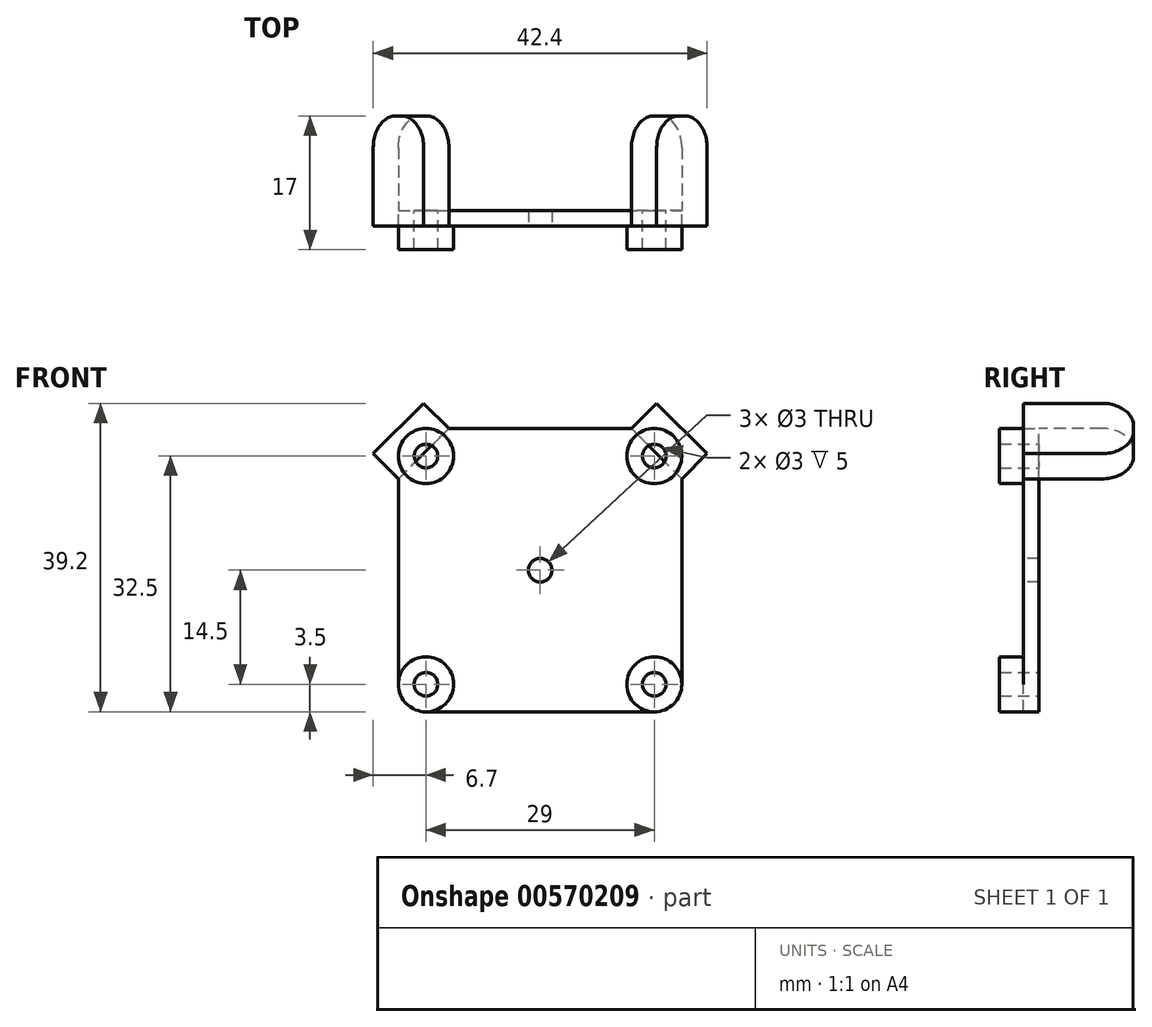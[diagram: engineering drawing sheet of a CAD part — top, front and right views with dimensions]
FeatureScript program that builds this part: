
annotation { "Feature Type Name" : "Feature", "Feature Type Description" : "" }
export const myFeature = defineFeature(function(context is Context, id is Id, definition is map)
    precondition{}
    {
        {
            var Q0;
            Q0=qCreatedBy(makeId("Front.planeOp"),FACE);
            var sketch = newSketch(context, id + "F0", { "sketchPlane" : qUnion([Q0])});
            skLineSegment(sketch, "E0.bottom", {"start": v(0, 0) * mm, "end": v(36, 0) * mm});
            skLineSegment(sketch, "E0.top", {"start": v(0, 36) * mm, "end": v(36, 36) * mm});
            skLineSegment(sketch, "E0.left", {"start": v(0, 0) * mm, "end": v(0, 36) * mm});
            skLineSegment(sketch, "E0.right", {"start": v(36, 0) * mm, "end": v(36, 36) * mm});
            skSolve(sketch);
        }
        {
            var Q0;
            Q0=makeQuery(id+"F0.imprint","IMPRINT",FACE,{"disambiguationData":[TD([[makeQuery(id+"F0.imprint","IMPRINT",EDGE,{"derivedFrom":sQuery(id+"F0.wireOp",EDGE,"E0.bottom")}),1.0]])]});
            extrude(context, id + "F1", {"entities" : qUnion([Q0]), "depth" : 2 * mm, "offsetDistance" : 25 * mm});
        }
        {
            var Q0;
            Q0=makeQuery(id+"F1.opExtrude","CAP_FACE",FACE,{"disambiguationData":[OSD([sQuery(id+"F0.wireOp",EDGE,"E0.bottom"),sQuery(id+"F0.wireOp",EDGE,"E0.top"),sQuery(id+"F0.wireOp",EDGE,"E0.left"),sQuery(id+"F0.wireOp",EDGE,"E0.right")])],"isStart":false});
            var sketch = newSketch(context, id + "F2", { "sketchPlane" : qUnion([Q0])});
            skCircle(sketch, "E1", {"center": v(3.5, 32.5) * mm, "radius": 3.5 * mm});
            skCircle(sketch, "E2", {"center": v(32.5, 32.5) * mm, "radius": 3.5 * mm});
            skCircle(sketch, "E3", {"center": v(32.5, 3.5) * mm, "radius": 3.5 * mm});
            skCircle(sketch, "E4", {"center": v(3.5, 3.5) * mm, "radius": 3.5 * mm});
            skCircle(sketch, "E5", {"center": v(3.5, 32.5) * mm, "radius": 1.5 * mm});
            skCircle(sketch, "E6", {"center": v(32.5, 32.5) * mm, "radius": 1.5 * mm});
            skCircle(sketch, "E7", {"center": v(32.5, 3.5) * mm, "radius": 1.5 * mm});
            skCircle(sketch, "E8", {"center": v(3.5, 3.5) * mm, "radius": 1.5 * mm});
            skSolve(sketch);
        }
        {
            var Q0;
            Q0 = qSketchRegion(id + "F2", true);
            extrude(context, id + "F3", {"entities" : qUnion([Q0]), "operationType" : NewBodyOperationType.ADD, "depth" : 3 * mm, "offsetDistance" : 25 * mm});
        }
        {
            var Q0;
            {var subQ0=sQuery(id+"F0.wireOp",EDGE,"E0.left");var subQ1=sQuery(id+"F0.wireOp",EDGE,"E0.top");var subQ2=sQuery(id+"F0.wireOp",EDGE,"E0.right");var subQ3=sQuery(id+"F0.wireOp",EDGE,"E0.bottom");var subQ4=makeQuery(id+"F1.opExtrude","CAP_FACE",FACE,{"disambiguationData":[OSD([subQ3,subQ1,subQ0,subQ2])],"isStart":false});Q0=makeQuery(id+"F3.boolean.opBoolean","SPLIT",FACE,{"disambiguationData":[TD([makeQuery(id+"F1.opExtrude","SWEPT_FACE",FACE,{"disambiguationData":[OSD([subQ3])]}),subQ4,makeQuery(id+"F1.opExtrude","SWEPT_FACE",FACE,{"disambiguationData":[OSD([subQ1])]}),makeQuery(id+"F1.opExtrude","SWEPT_FACE",FACE,{"disambiguationData":[OSD([subQ0])]}),makeQuery(id+"F1.opExtrude","SWEPT_FACE",FACE,{"disambiguationData":[OSD([subQ2])]}),makeQuery(id+"F3.opExtrude","SWEPT_FACE",FACE,{"disambiguationData":[OSD([sQuery(id+"F2.wireOp",EDGE,"E1")])]}),makeQuery(id+"F3.opExtrude","SWEPT_FACE",FACE,{"disambiguationData":[OSD([sQuery(id+"F2.wireOp",EDGE,"E2")])]}),makeQuery(id+"F3.opExtrude","SWEPT_FACE",FACE,{"disambiguationData":[OSD([sQuery(id+"F2.wireOp",EDGE,"E3")])]}),makeQuery(id+"F3.opExtrude","SWEPT_FACE",FACE,{"disambiguationData":[OSD([sQuery(id+"F2.wireOp",EDGE,"E4")])]})])],"derivedFrom":subQ4});}
            var sketch = newSketch(context, id + "F4", { "sketchPlane" : qUnion([Q0])});
            skCircle(sketch, "E9", {"center": v(18, 18) * mm, "radius": 1.5 * mm});
            skLineSegment(sketch, "E10", {"start": v(18, 18) * mm, "end": v(36, 18) * mm, "construction": true});
            skLineSegment(sketch, "E11", {"start": v(18, 18) * mm, "end": v(18, 36) * mm, "construction": true});
            skSolve(sketch);
        }
        {
            var Q0;
            Q0=makeQuery(id+"F3.boolean.opBoolean","SPLIT",FACE,{"disambiguationData":[TD([makeQuery(id+"F3.opExtrude","SWEPT_FACE",FACE,{"disambiguationData":[OSD([sQuery(id+"F2.wireOp",EDGE,"E5")])]})])],"derivedFrom":makeQuery(id+"F1.opExtrude","CAP_FACE",FACE,{"disambiguationData":[OSD([sQuery(id+"F0.wireOp",EDGE,"E0.bottom"),sQuery(id+"F0.wireOp",EDGE,"E0.top"),sQuery(id+"F0.wireOp",EDGE,"E0.left"),sQuery(id+"F0.wireOp",EDGE,"E0.right")])],"isStart":false})});
            var Q1;
            Q1=makeQuery(id+"F3.boolean.opBoolean","SPLIT",FACE,{"disambiguationData":[TD([makeQuery(id+"F3.opExtrude","SWEPT_FACE",FACE,{"disambiguationData":[OSD([sQuery(id+"F2.wireOp",EDGE,"E8")])]})])],"derivedFrom":makeQuery(id+"F1.opExtrude","CAP_FACE",FACE,{"disambiguationData":[OSD([sQuery(id+"F0.wireOp",EDGE,"E0.bottom"),sQuery(id+"F0.wireOp",EDGE,"E0.top"),sQuery(id+"F0.wireOp",EDGE,"E0.left"),sQuery(id+"F0.wireOp",EDGE,"E0.right")])],"isStart":false})});
            var Q2;
            Q2=makeQuery(id+"F3.boolean.opBoolean","SPLIT",FACE,{"disambiguationData":[TD([makeQuery(id+"F3.opExtrude","SWEPT_FACE",FACE,{"disambiguationData":[OSD([sQuery(id+"F2.wireOp",EDGE,"E7")])]})])],"derivedFrom":makeQuery(id+"F1.opExtrude","CAP_FACE",FACE,{"disambiguationData":[OSD([sQuery(id+"F0.wireOp",EDGE,"E0.bottom"),sQuery(id+"F0.wireOp",EDGE,"E0.top"),sQuery(id+"F0.wireOp",EDGE,"E0.left"),sQuery(id+"F0.wireOp",EDGE,"E0.right")])],"isStart":false})});
            var Q3;
            Q3=makeQuery(id+"F3.boolean.opBoolean","SPLIT",FACE,{"disambiguationData":[TD([makeQuery(id+"F3.opExtrude","SWEPT_FACE",FACE,{"disambiguationData":[OSD([sQuery(id+"F2.wireOp",EDGE,"E6")])]})])],"derivedFrom":makeQuery(id+"F1.opExtrude","CAP_FACE",FACE,{"disambiguationData":[OSD([sQuery(id+"F0.wireOp",EDGE,"E0.bottom"),sQuery(id+"F0.wireOp",EDGE,"E0.top"),sQuery(id+"F0.wireOp",EDGE,"E0.left"),sQuery(id+"F0.wireOp",EDGE,"E0.right")])],"isStart":false})});
            var Q4;
            Q4=makeQuery(id+"F4.imprint","IMPRINT",FACE,{"disambiguationData":[TD([[makeQuery(id+"F4.imprint","IMPRINT",EDGE,{"derivedFrom":sQuery(id+"F4.wireOp",EDGE,"E9")}),1.0]])]});
            var Q5;
            Q5=makeQuery(id+"F1.opExtrude","CAP_FACE",FACE,{"disambiguationData":[OSD([sQuery(id+"F0.wireOp",EDGE,"E0.bottom"),sQuery(id+"F0.wireOp",EDGE,"E0.top"),sQuery(id+"F0.wireOp",EDGE,"E0.left"),sQuery(id+"F0.wireOp",EDGE,"E0.right")])],"isStart":true});
            extrude(context, id + "F5", {"entities" : qUnion([Q0, Q1, Q2, Q3, Q4]), "operationType" : NewBodyOperationType.REMOVE, "endBound" : BoundingType.UP_TO_SURFACE, "oppositeDirection" : true, "depth" : 25 * mm, "endBoundEntityFace" : qUnion([Q5]), "offsetDistance" : 25 * mm});
        }
        {
            var Q0;
            Q0=makeQuery(id+"F1.opExtrude","CAP_FACE",FACE,{"disambiguationData":[OSD([sQuery(id+"F0.wireOp",EDGE,"E0.bottom"),sQuery(id+"F0.wireOp",EDGE,"E0.top"),sQuery(id+"F0.wireOp",EDGE,"E0.left"),sQuery(id+"F0.wireOp",EDGE,"E0.right")])],"isStart":true});
            var sketch = newSketch(context, id + "F6", { "sketchPlane" : qUnion([Q0])});
            skLineSegment(sketch, "E12", {"start": v(-36, 29.6) * mm, "end": v(-29.6, 36) * mm});
            skPoint(sketch, "E13", {"position": v(-32.8, 32.8) * mm});
            skCircle(sketch, "E14.0", {"center": v(-32.5, 32.5) * mm, "radius": 1.5 * mm, "construction": true});
            skLineSegment(sketch, "E15", {"start": v(0, 29.6) * mm, "end": v(-6.4, 36) * mm});
            skPoint(sketch, "E16", {"position": v(-3.2, 32.8) * mm});
            skLineSegment(sketch, "E17", {"start": v(-36, 29.6) * mm, "end": v(-39.2, 32.8) * mm});
            skPoint(sketch, "E17.endSnap0", {"position": v(-36, 32.8) * mm});
            skLineSegment(sketch, "E18", {"start": v(-39.2, 32.8) * mm, "end": v(-32.8, 39.2) * mm});
            skPoint(sketch, "E19", {"position": v(0, 32.8) * mm});
            skLineSegment(sketch, "E20", {"start": v(0, 29.6) * mm, "end": v(3.2, 32.8) * mm});
            skLineSegment(sketch, "E21", {"start": v(3.2, 32.8) * mm, "end": v(-3.2, 39.2) * mm});
            skPoint(sketch, "E22.orphan", {"position": v(0, 36) * mm});
            skLineSegment(sketch, "E23", {"start": v(-29.6, 36) * mm, "end": v(-32.8, 39.2) * mm});
            skLineSegment(sketch, "E24", {"start": v(-6.4, 36) * mm, "end": v(-3.2, 39.2) * mm});
            skSolve(sketch);
        }
        {
            var Q0;
            Q0 = qSketchRegion(id + "F6", true);
            extrude(context, id + "F7", {"entities" : qUnion([Q0]), "operationType" : NewBodyOperationType.ADD, "depth" : 12 * mm, "offsetDistance" : 25 * mm});
        }
        {
            var Q0;
            Q0=makeQuery(id+"F1.opExtrude","CAP_FACE",FACE,{"disambiguationData":[OSD([sQuery(id+"F0.wireOp",EDGE,"E0.bottom"),sQuery(id+"F0.wireOp",EDGE,"E0.top"),sQuery(id+"F0.wireOp",EDGE,"E0.left"),sQuery(id+"F0.wireOp",EDGE,"E0.right")])],"isStart":true});
            var sketch = newSketch(context, id + "F8", { "sketchPlane" : qUnion([Q0])});
            skLineSegment(sketch, "E25.top", {"start": v(-29.6, 29.6) * mm, "end": v(-36, 29.6) * mm});
            skLineSegment(sketch, "E25.left", {"start": v(-29.6, 36) * mm, "end": v(-29.6, 29.6) * mm});
            skLineSegment(sketch, "E26.bottom", {"start": v(0, 29.6) * mm, "end": v(-6.4, 29.6) * mm});
            skLineSegment(sketch, "E26.right", {"start": v(-6.4, 29.6) * mm, "end": v(-6.4, 36) * mm});
            skLineSegment(sketch, "E27.0", {"start": v(-2.18, 31.78) * mm, "end": v(-4.22, 33.82) * mm});
            skLineSegment(sketch, "E28.0", {"start": v(0, 29.6) * mm, "end": v(-2.18, 31.78) * mm});
            skLineSegment(sketch, "E29.0", {"start": v(-4.22, 33.82) * mm, "end": v(-6.4, 36) * mm});
            skLineSegment(sketch, "E30.0", {"start": v(-36, 29.6) * mm, "end": v(-33.82, 31.78) * mm});
            skLineSegment(sketch, "E31.0", {"start": v(-33.82, 31.78) * mm, "end": v(-31.78, 33.82) * mm});
            skLineSegment(sketch, "E32.0", {"start": v(-31.78, 33.82) * mm, "end": v(-29.6, 36) * mm});
            skSolve(sketch);
        }
        {
            var Q0;
            {var subQ2=sQuery(id+"F6.wireOp",EDGE,"E12");var subQ3=sQuery(id+"F6.wireOp",EDGE,"E18");var subQ4=sQuery(id+"F6.wireOp",EDGE,"E17");var subQ5=makeQuery(id+"F7.opExtrude","CAP_FACE",FACE,{"disambiguationData":[OSD([subQ2,subQ4,subQ3,sQuery(id+"F6.wireOp",EDGE,"E23")])],"isStart":true});Q0=makeQuery(id+"F7.boolean.opBoolean","SPLIT",FACE,{"disambiguationData":[TD([makeQuery(id+"F7.opExtrude","SWEPT_FACE",FACE,{"disambiguationData":[OSD([subQ4])]})])],"derivedFrom":subQ5});}
            var Q1;
            {var subQ2=sQuery(id+"F6.wireOp",EDGE,"E12");var subQ3=sQuery(id+"F6.wireOp",EDGE,"E23");var subQ4=sQuery(id+"F6.wireOp",EDGE,"E18");var subQ5=makeQuery(id+"F7.opExtrude","CAP_FACE",FACE,{"disambiguationData":[OSD([subQ2,sQuery(id+"F6.wireOp",EDGE,"E17"),subQ4,subQ3])],"isStart":true});Q1=makeQuery(id+"F7.boolean.opBoolean","SPLIT",FACE,{"disambiguationData":[TD([makeQuery(id+"F7.opExtrude","SWEPT_FACE",FACE,{"disambiguationData":[OSD([subQ3])]})])],"derivedFrom":subQ5});}
            var Q2;
            {var subQ0=sQuery(id+"F6.wireOp",EDGE,"E15");var subQ3=sQuery(id+"F6.wireOp",EDGE,"E24");var subQ4=sQuery(id+"F6.wireOp",EDGE,"E21");var subQ5=makeQuery(id+"F7.opExtrude","CAP_FACE",FACE,{"disambiguationData":[OSD([subQ0,sQuery(id+"F6.wireOp",EDGE,"E20"),subQ4,subQ3])],"isStart":true});Q2=makeQuery(id+"F7.boolean.opBoolean","SPLIT",FACE,{"disambiguationData":[TD([makeQuery(id+"F7.opExtrude","SWEPT_FACE",FACE,{"disambiguationData":[OSD([subQ3])]})])],"derivedFrom":subQ5});}
            var Q3;
            {var subQ0=sQuery(id+"F6.wireOp",EDGE,"E15");var subQ3=sQuery(id+"F6.wireOp",EDGE,"E21");var subQ4=sQuery(id+"F6.wireOp",EDGE,"E20");var subQ5=makeQuery(id+"F7.opExtrude","CAP_FACE",FACE,{"disambiguationData":[OSD([subQ0,subQ4,subQ3,sQuery(id+"F6.wireOp",EDGE,"E24")])],"isStart":true});Q3=makeQuery(id+"F7.boolean.opBoolean","SPLIT",FACE,{"disambiguationData":[TD([makeQuery(id+"F7.opExtrude","SWEPT_FACE",FACE,{"disambiguationData":[OSD([subQ4])]})])],"derivedFrom":subQ5});}
            var Q4;
            {var subQ0=sQuery(id+"F0.wireOp",EDGE,"E0.left");var subQ1=sQuery(id+"F0.wireOp",EDGE,"E0.top");var subQ2=sQuery(id+"F0.wireOp",EDGE,"E0.right");var subQ3=sQuery(id+"F0.wireOp",EDGE,"E0.bottom");var subQ4=makeQuery(id+"F1.opExtrude","CAP_FACE",FACE,{"disambiguationData":[OSD([subQ3,subQ1,subQ0,subQ2])],"isStart":false});Q4=makeQuery(id+"F3.boolean.opBoolean","SPLIT",FACE,{"disambiguationData":[TD([makeQuery(id+"F1.opExtrude","SWEPT_FACE",FACE,{"disambiguationData":[OSD([subQ3])]}),subQ4,makeQuery(id+"F1.opExtrude","SWEPT_FACE",FACE,{"disambiguationData":[OSD([subQ1])]}),makeQuery(id+"F1.opExtrude","SWEPT_FACE",FACE,{"disambiguationData":[OSD([subQ0])]}),makeQuery(id+"F1.opExtrude","SWEPT_FACE",FACE,{"disambiguationData":[OSD([subQ2])]}),makeQuery(id+"F3.opExtrude","SWEPT_FACE",FACE,{"disambiguationData":[OSD([sQuery(id+"F2.wireOp",EDGE,"E1")])]}),makeQuery(id+"F3.opExtrude","SWEPT_FACE",FACE,{"disambiguationData":[OSD([sQuery(id+"F2.wireOp",EDGE,"E2")])]}),makeQuery(id+"F3.opExtrude","SWEPT_FACE",FACE,{"disambiguationData":[OSD([sQuery(id+"F2.wireOp",EDGE,"E3")])]}),makeQuery(id+"F3.opExtrude","SWEPT_FACE",FACE,{"disambiguationData":[OSD([sQuery(id+"F2.wireOp",EDGE,"E4")])]})])],"derivedFrom":subQ4});}
            extrude(context, id + "F9", {"entities" : qUnion([Q0, Q1, Q2, Q3]), "operationType" : NewBodyOperationType.ADD, "endBound" : BoundingType.UP_TO_SURFACE, "depth" : 25 * mm, "endBoundEntityFace" : qUnion([Q4]), "offsetDistance" : 25 * mm});
        }
        {
            var Q0;
            Q0=makeQuery(id+"F7.opExtrude","SWEPT_FACE",FACE,{"disambiguationData":[OSD([sQuery(id+"F6.wireOp",EDGE,"E12")])]});
            var sketch = newSketch(context, id + "F10", { "sketchPlane" : qUnion([Q0])});
            skCircle(sketch, "E33", {"center": v(0, -8) * mm, "radius": 1.5 * mm});
            skPoint(sketch, "E33.centerSnap0", {"position": v(0, -12) * mm});
            skLineSegment(sketch, "E34.0", {"start": v(-2.47, 2) * mm, "end": v(-20.93, 2) * mm, "construction": true});
            skSolve(sketch);
        }
        {
            var Q0;
            Q0 = qSketchRegion(id + "F10", true);
            var Q1;
            {var subQ0=sQuery(id+"F6.wireOp",EDGE,"E18");var subQ1=makeQuery(id+"F7.opExtrude","SWEPT_FACE",FACE,{"disambiguationData":[OSD([subQ0])]});var subQ2=sQuery(id+"F6.wireOp",EDGE,"E23");var subQ3=sQuery(id+"F6.wireOp",EDGE,"E17");var subQ7=makeQuery(id+"F7.opExtrude","CAP_EDGE",EDGE,{"disambiguationData":[OSD([subQ0])],"isStart":true});Q1=makeQuery(id+"F9.boolean.opBoolean","MERGE",FACE,{"derivedFrom":[subQ1,makeQuery(id+"F9.opExtrude","SWEPT_FACE",FACE,{"disambiguationData":[OSD([subQ0]),TDD([makeQuery(id+"F7.boolean.opBoolean","SPLIT",EDGE,{"disambiguationData":[TD([makeQuery(id+"F7.opExtrude","SWEPT_FACE",FACE,{"disambiguationData":[OSD([subQ3])]})])],"derivedFrom":subQ7})])]}),makeQuery(id+"F9.opExtrude","SWEPT_FACE",FACE,{"disambiguationData":[OSD([subQ0]),TDD([makeQuery(id+"F7.boolean.opBoolean","SPLIT",EDGE,{"disambiguationData":[TD([makeQuery(id+"F7.opExtrude","SWEPT_FACE",FACE,{"disambiguationData":[OSD([subQ2])]})])],"derivedFrom":subQ7})])]})]});}
            extrude(context, id + "F11", {"entities" : qUnion([Q0]), "operationType" : NewBodyOperationType.REMOVE, "endBound" : BoundingType.UP_TO_SURFACE, "oppositeDirection" : true, "depth" : 25 * mm, "endBoundEntityFace" : qUnion([Q1]), "offsetDistance" : 25 * mm});
        }
        {
            var Q0;
            Q0=makeQuery(id+"F7.opExtrude","SWEPT_FACE",FACE,{"disambiguationData":[OSD([sQuery(id+"F6.wireOp",EDGE,"E15")])]});
            var sketch = newSketch(context, id + "F12", { "sketchPlane" : qUnion([Q0])});
            skCircle(sketch, "E35", {"center": v(25.46, -8) * mm, "radius": 1.5 * mm});
            skLineSegment(sketch, "E36.0", {"start": v(2.47, 2) * mm, "end": v(22.98, 2) * mm, "construction": true});
            skLineSegment(sketch, "E37.0", {"start": v(20.93, -12) * mm, "end": v(29.98, -12) * mm, "construction": true});
            skPoint(sketch, "E38", {"position": v(25.46, -12) * mm});
            skSolve(sketch);
        }
        {
            var Q0;
            Q0 = qSketchRegion(id + "F12", true);
            var Q1;
            {var subQ0=sQuery(id+"F6.wireOp",EDGE,"E21");var subQ1=makeQuery(id+"F7.opExtrude","SWEPT_FACE",FACE,{"disambiguationData":[OSD([subQ0])]});var subQ3=sQuery(id+"F6.wireOp",EDGE,"E24");var subQ4=sQuery(id+"F6.wireOp",EDGE,"E20");var subQ7=makeQuery(id+"F7.opExtrude","CAP_EDGE",EDGE,{"disambiguationData":[OSD([subQ0])],"isStart":true});Q1=makeQuery(id+"F9.boolean.opBoolean","MERGE",FACE,{"derivedFrom":[subQ1,makeQuery(id+"F9.opExtrude","SWEPT_FACE",FACE,{"disambiguationData":[OSD([subQ0]),TDD([makeQuery(id+"F7.boolean.opBoolean","SPLIT",EDGE,{"disambiguationData":[TD([makeQuery(id+"F7.opExtrude","SWEPT_FACE",FACE,{"disambiguationData":[OSD([subQ4])]})])],"derivedFrom":subQ7})])]}),makeQuery(id+"F9.opExtrude","SWEPT_FACE",FACE,{"disambiguationData":[OSD([subQ0]),TDD([makeQuery(id+"F7.boolean.opBoolean","SPLIT",EDGE,{"disambiguationData":[TD([makeQuery(id+"F7.opExtrude","SWEPT_FACE",FACE,{"disambiguationData":[OSD([subQ3])]})])],"derivedFrom":subQ7})])]})]});}
            extrude(context, id + "F13", {"entities" : qUnion([Q0]), "operationType" : NewBodyOperationType.REMOVE, "endBound" : BoundingType.UP_TO_SURFACE, "oppositeDirection" : true, "depth" : 25 * mm, "endBoundEntityFace" : qUnion([Q1]), "offsetDistance" : 25 * mm});
        }
        {
            var Q0;
            Q0=makeQuery(id+"F7.opExtrude","CAP_EDGE",EDGE,{"disambiguationData":[OSD([sQuery(id+"F6.wireOp",EDGE,"E20")])],"isStart":false});
            var Q1;
            Q1=makeQuery(id+"F7.opExtrude","CAP_EDGE",EDGE,{"disambiguationData":[OSD([sQuery(id+"F6.wireOp",EDGE,"E24")])],"isStart":false});
            var Q2;
            Q2=makeQuery(id+"F7.opExtrude","CAP_EDGE",EDGE,{"disambiguationData":[OSD([sQuery(id+"F6.wireOp",EDGE,"E23")])],"isStart":false});
            var Q3;
            Q3=makeQuery(id+"F7.opExtrude","CAP_EDGE",EDGE,{"disambiguationData":[OSD([sQuery(id+"F6.wireOp",EDGE,"E17")])],"isStart":false});
            fillet(context, id + "F14", {"entities" : qUnion([Q0, Q1, Q2, Q3]), "radius" : 4 * mm, "tangentPropagation" : true, "allowEdgeOverflow" : false});
        }
        {
            var Q0;
            Q0=makeQuery(id+"F1.opExtrude","SWEPT_EDGE",EDGE,{"disambiguationData":[OSD([sQuery(id+"F0.wireOp",EDGE,"E0.bottom"),sQuery(id+"F0.wireOp",EDGE,"E0.left")])]});
            var Q1;
            Q1=makeQuery(id+"F1.opExtrude","SWEPT_EDGE",EDGE,{"disambiguationData":[OSD([sQuery(id+"F0.wireOp",EDGE,"E0.bottom"),sQuery(id+"F0.wireOp",EDGE,"E0.right")])]});
            fillet(context, id + "F15", {"entities" : qUnion([Q0, Q1]), "radius" : 3.5 * mm, "tangentPropagation" : true, "allowEdgeOverflow" : false});
        }
    });
